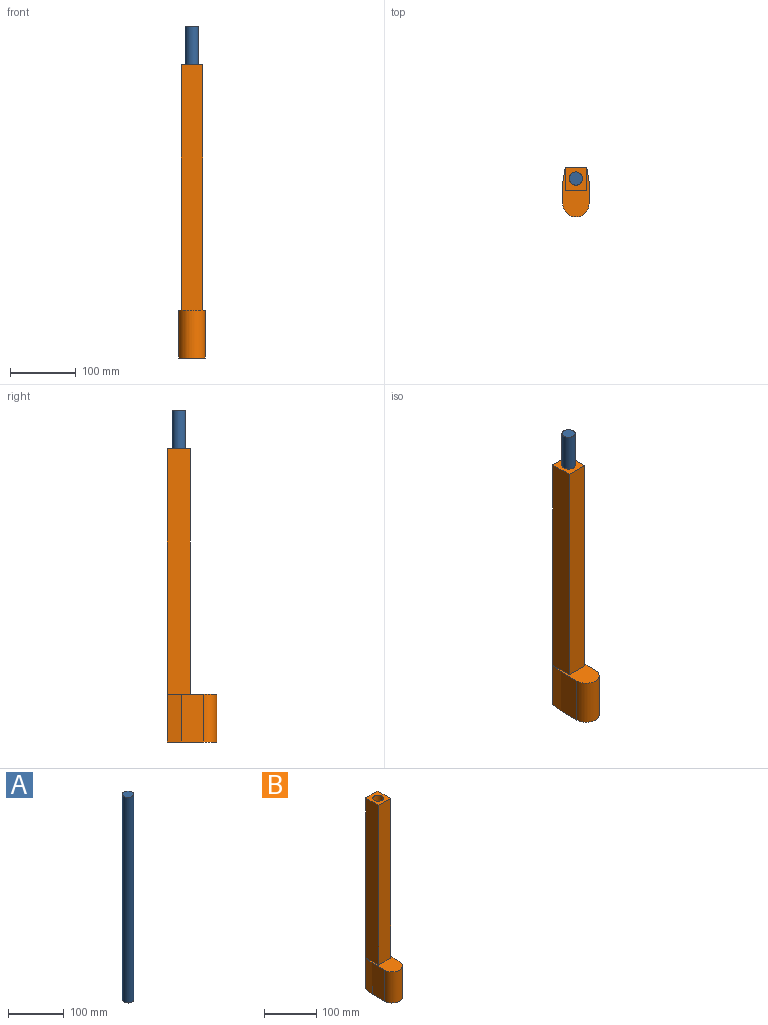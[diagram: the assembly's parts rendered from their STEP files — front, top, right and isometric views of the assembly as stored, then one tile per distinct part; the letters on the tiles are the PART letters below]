
ASSEMBLY  parts=2 mates=1
PART A: 3 faces, bbox 20x20x453.3 mm
  f0: cylinder r=10mm len=453.26mm, axis (0,0,-1), area 28479.4mm2, adj f1,f2
  f1: plane 20x20mm, normal (0,0,1), area 314.2mm2, adj f0
  f2: plane 20x20mm, normal (0,0,-1), area 314.2mm2, adj f0
PART B: 18 faces, bbox 40x75x445.4 mm
  f0: plane 35x0.22mm, normal (0,0,1), area 3.9mm2, adj f7,f12,f15
  f1: plane 33.82x0.13mm, normal (0,0,1), area 0.7mm2, adj f4,f5,f14
  f2: plane 72.6x33.82mm, normal (-1,0,0), area 2455.4mm2, adj f3,f8,f9,f16
  f3: cylinder r=19.94mm len=72.6mm, axis (0,0,-1), area 4531mm2, adj f2,f4,f9,f14,f16
  f4: plane 25.4x22.39mm, normal (1,-0.01,0), area 568.8mm2, adj f1,f3,f5,f9
  f5: plane 25.4x11.43mm, normal (1,0,0), area 290.3mm2, adj f1,f4,f6,f9
  f6: plane 72.6x21.35mm, normal (0.99,0.17,0), area 1573.1mm2, adj f5,f7,f9,f14,f15,f16
  f7: plane 445.4x32.66mm, normal (0,1,0), area 14451.8mm2, adj f0,f6,f8,f9,f10,f12,f13
  f8: plane 72.6x21.35mm, normal (-0.99,0.17,0), area 1573.1mm2, adj f2,f7,f9,f16
  f9: plane 75x40mm, normal (0,0,-1), area 2433mm2, adj f2,f3,f4,f5,f6,f7,f8,f17
  f10: plane 372.8x35mm, normal (-1,0,0), area 13048mm2, adj f7,f11,f13,f16
  f11: plane 372.8x32.43mm, normal (0,-1,0), area 12091.4mm2, adj f10,f12,f13,f16
  f12: plane 420x35mm, normal (1,0,0), area 14700mm2, adj f0,f7,f11,f13,f15
  f13: plane 35x32.43mm, normal (0,0,1), area 821mm2, adj f7,f10,f11,f12,f17
  f14: plane 47.2x33.82mm, normal (1,0,0), area 1596.3mm2, adj f1,f3,f6,f16
  f15: plane 47.2x35mm, normal (-1,0.01,0), area 1652mm2, adj f0,f6,f12,f16
  f16: plane 75x40mm, normal (0,0,1), area 1607.3mm2, adj f2,f3,f6,f8,f10,f11,f14,f15
  f17: cylinder r=10mm len=445.4mm, axis (0,0,1), area 27985.3mm2, adj f9,f13
PLACE A t=(-161.33,110.56,59.54)mm
PLACE B t=(-161.74,67.07,8.35)mm fixed
MATE slider A.f0 <-> B.f17  axis (0,0,-1) through (-161.33,110.56,286.18)mm
